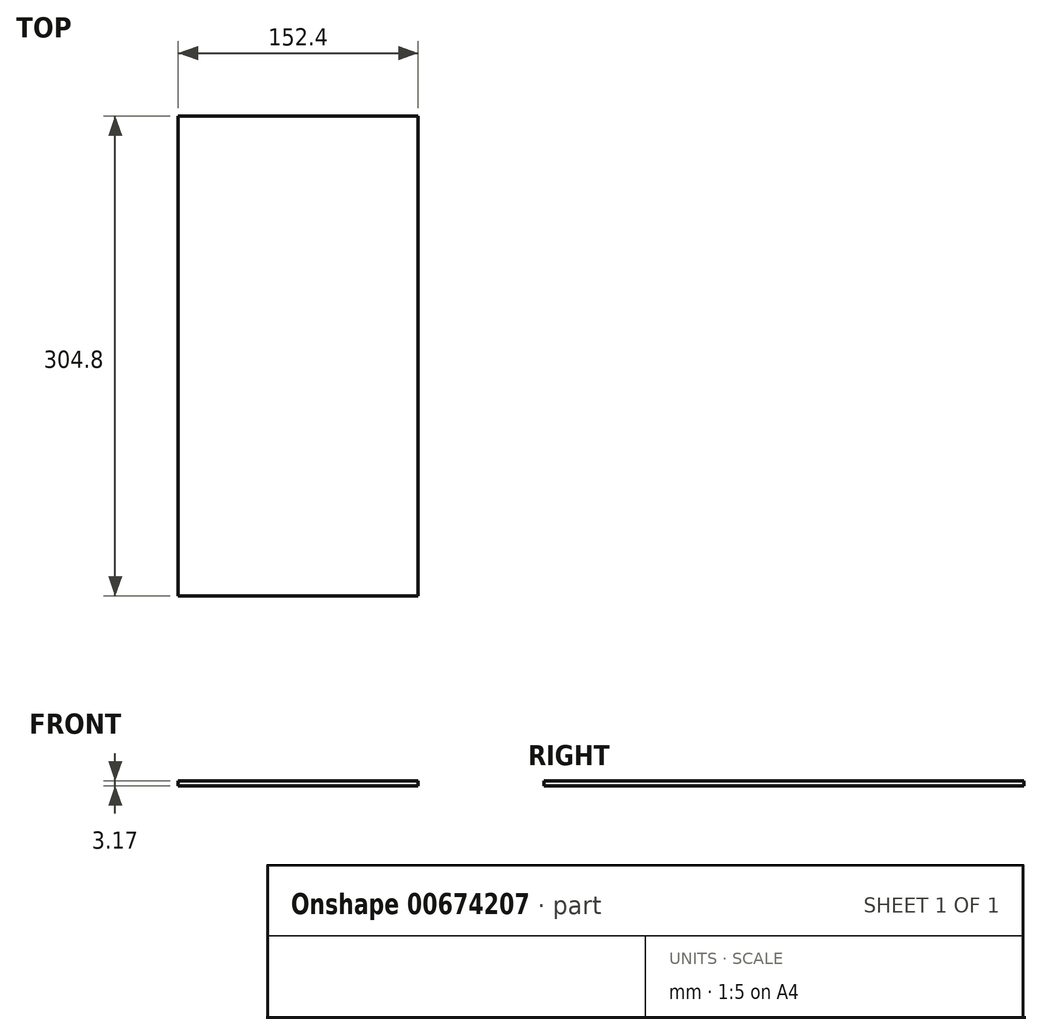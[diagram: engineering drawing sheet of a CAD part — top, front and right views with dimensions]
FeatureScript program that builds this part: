
annotation { "Feature Type Name" : "Feature", "Feature Type Description" : "" }
export const myFeature = defineFeature(function(context is Context, id is Id, definition is map)
    precondition{}
    {
        {
            var Q0;
            Q0=qCreatedBy(makeId("Top.planeOp"),FACE);
            var sketch = newSketch(context, id + "F0", { "sketchPlane" : qUnion([Q0])});
            skLineSegment(sketch, "E0.bottom", {"start": v(76.2, 152.4) * mm, "end": v(-76.2, 152.4) * mm});
            skLineSegment(sketch, "E0.top", {"start": v(76.2, -152.4) * mm, "end": v(-76.2, -152.4) * mm});
            skLineSegment(sketch, "E0.left", {"start": v(76.2, 152.4) * mm, "end": v(76.2, -152.4) * mm});
            skLineSegment(sketch, "E0.right", {"start": v(-76.2, 152.4) * mm, "end": v(-76.2, -152.4) * mm});
            skPoint(sketch, "E0.middle", {"position": v(0, 0) * mm});
            skSolve(sketch);
        }
        {
            var Q0;
            Q0=makeQuery(id+"F0.imprint","IMPRINT",FACE,{"disambiguationData":[TD([[makeQuery(id+"F0.imprint","IMPRINT",EDGE,{"derivedFrom":sQuery(id+"F0.wireOp",EDGE,"E0.bottom")}),1.0]])]});
            extrude(context, id + "F1", {"entities" : qUnion([Q0]), "depth" : 3.17 * mm, "offsetDistance" : 25.4 * mm});
        }
    });
